# Revit family: Seating-Casual-Naughtone-VIV-CH-WD
name_source: partatom
category: Furniture
revit_build: Autodesk Revit 2014 (Build: 20140709_2115(x64)
units: mm (PartAtom-declared; Revit-internal decimal feet)

## types (1)
- VIV-CH-WD
    Additional Materials = Additional material and finish options available. Please contact Naughtone direct for further information.
    AssetIdentifier = VIV-CH-WD
    Barcode = 0
    COBie Description = Designed by Naughtone, The Viv chair's paired down shape is highlighted by its tight upholstery, cleverly held deeply in to the bucketed seat. Viv was motivated by quality and function and the range of chair, barstool and lounge chair are a welcome addition to any space, especially as their fully upholstered form can be easily altered with a change of fabrics.
    Cost = 0 $
    Current Revision = 1
    Depth = 560 mm  [stored 1.83727 ft]
    Description = Viv Chair with Timber Base
    Height = 780 mm  [stored 2.55906 ft]
    Length = 515 mm  [stored 1.68963 ft]
    Manufacturer = Naughtone
    Model = Viv Chair with Timber Base
    Name = Furniture-Seating-Casual-Naughtone-Viv
    Product Code = VIV-CH-WD
    Product URL = http://www.naughtone.com
    SerialNumber = 0
    TagNumber = 0
    TypeName = 515mmx560mmx780mm, Viv Chair
    URL = http://www.naughtone.com
    Uniclass = Pr_40_50_12
    WarrantyDuration = 60

note: [stored X ft] marks values corroborated as IEEE doubles in the binary element streams (Revit-internal decimal feet)

## geometry (parser evidence)
native form markers: Blend x1, Sweep x3
no freeform markers — native parametric forms only
